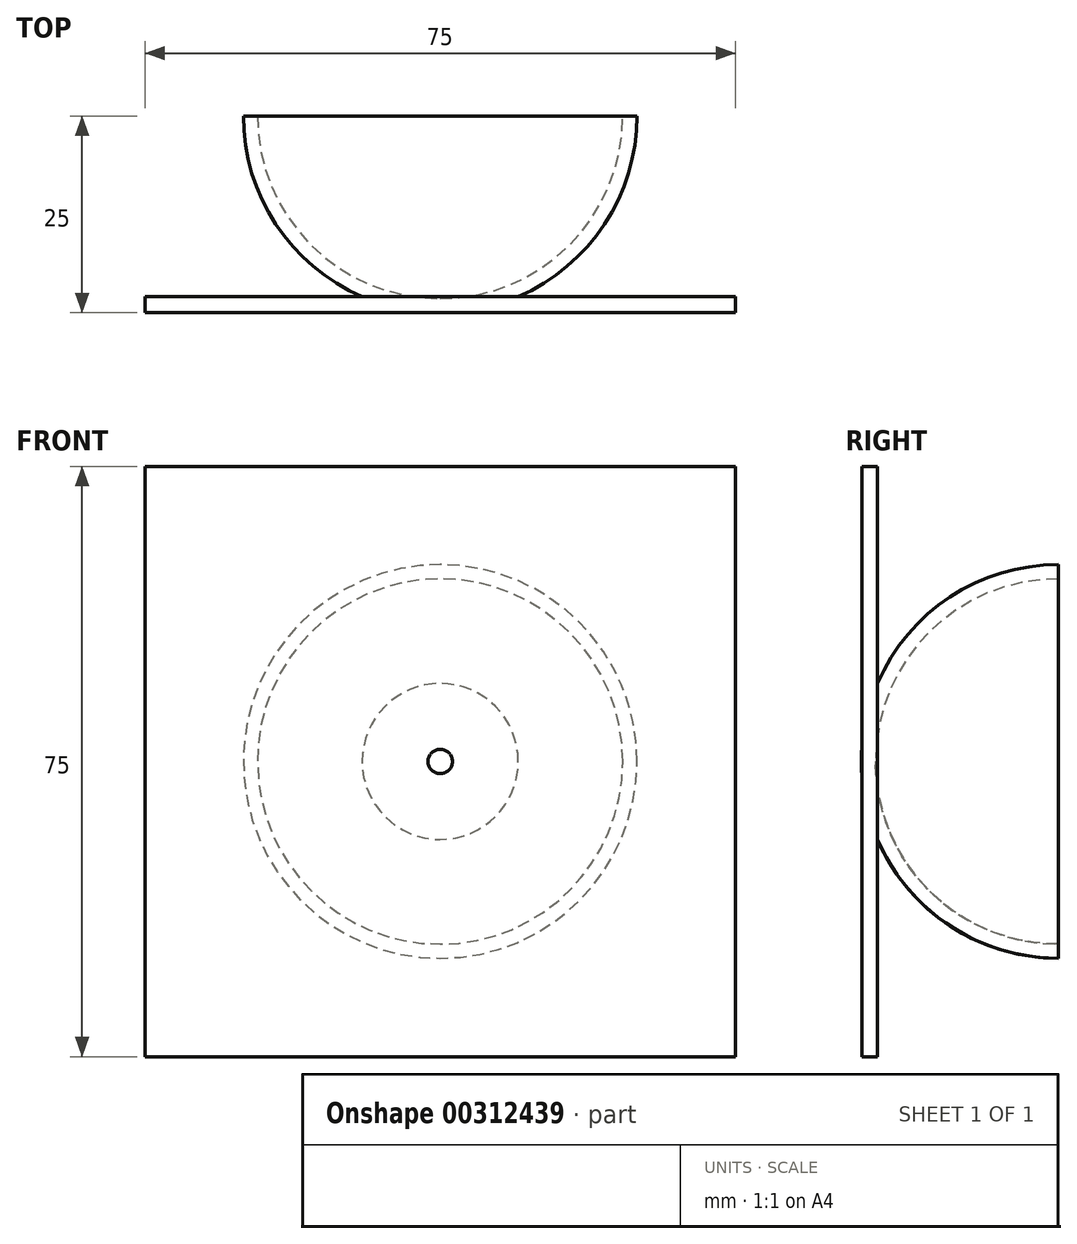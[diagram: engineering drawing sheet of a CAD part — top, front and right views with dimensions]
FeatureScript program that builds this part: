
annotation { "Feature Type Name" : "Feature", "Feature Type Description" : "" }
export const myFeature = defineFeature(function(context is Context, id is Id, definition is map)
    precondition{}
    {
        {
            var Q0;
            Q0=qCreatedBy(makeId("Right.planeOp"),FACE);
            var sketch = newSketch(context, id + "F0", { "sketchPlane" : qUnion([Q0])});
            skPoint(sketch, "E0.start.orphan", {"position": v(22.95, 0) * mm});
            skArc(sketch, "E1", {"start": v(-2.05, 0) * mm, "mid": v(5.27, -17.68) * mm, "end": v(22.95, -25) * mm});
            skLineSegment(sketch, "E2", {"start": v(-2.05, 0) * mm, "end": v(22.95, 0) * mm});
            skLineSegment(sketch, "E3", {"start": v(22.95, 0) * mm, "end": v(22.95, -25) * mm});
            skSolve(sketch);
        }
        {
            var Q0;
            Q0=makeQuery(id+"F0.imprint","IMPRINT",FACE,{"disambiguationData":[TD([[makeQuery(id+"F0.imprint","IMPRINT",EDGE,{"derivedFrom":sQuery(id+"F0.wireOp",EDGE,"E1")}),1.0]])]});
            var Q1;
            Q1=sQuery(id+"F0.wireOp",EDGE,"E2");
            revolve(context, id + "F1", {"entities" : qUnion([Q0]), "axis" : qUnion([Q1]), "revolveType" : RevolveType.FULL});
        }
        {
            var Q0;
            Q0=qCreatedBy(makeId("Front.planeOp"),FACE);
            var sketch = newSketch(context, id + "F2", { "sketchPlane" : qUnion([Q0])});
            skLineSegment(sketch, "E4.bottom", {"start": v(-37.5, 37.5) * mm, "end": v(37.5, 37.5) * mm});
            skLineSegment(sketch, "E4.top", {"start": v(-37.5, -37.5) * mm, "end": v(37.5, -37.5) * mm});
            skLineSegment(sketch, "E4.left", {"start": v(-37.5, 37.5) * mm, "end": v(-37.5, -37.5) * mm});
            skLineSegment(sketch, "E4.right", {"start": v(37.5, 37.5) * mm, "end": v(37.5, -37.5) * mm});
            skPoint(sketch, "E4.middle", {"position": v(0, 0) * mm});
            skSolve(sketch);
        }
        {
            var Q0;
            Q0=makeQuery(id+"F2.imprint","IMPRINT",FACE,{"disambiguationData":[TD([[makeQuery(id+"F2.imprint","IMPRINT",EDGE,{"derivedFrom":sQuery(id+"F2.wireOp",EDGE,"E4.bottom")}),-1.0]])]});
            extrude(context, id + "F3", {"entities" : qUnion([Q0]), "operationType" : NewBodyOperationType.ADD, "depth" : 2 * mm});
        }
        {
            var Q0;
            Q0=makeQuery(id+"F1.opRevolve","SWEPT_FACE",FACE,{"disambiguationData":[OSD([sQuery(id+"F0.wireOp",EDGE,"E3")])]});
            shell(context, id + "F4", {"entities" : qUnion([Q0]), "thickness" : 1.8 * mm});
        }
    });
